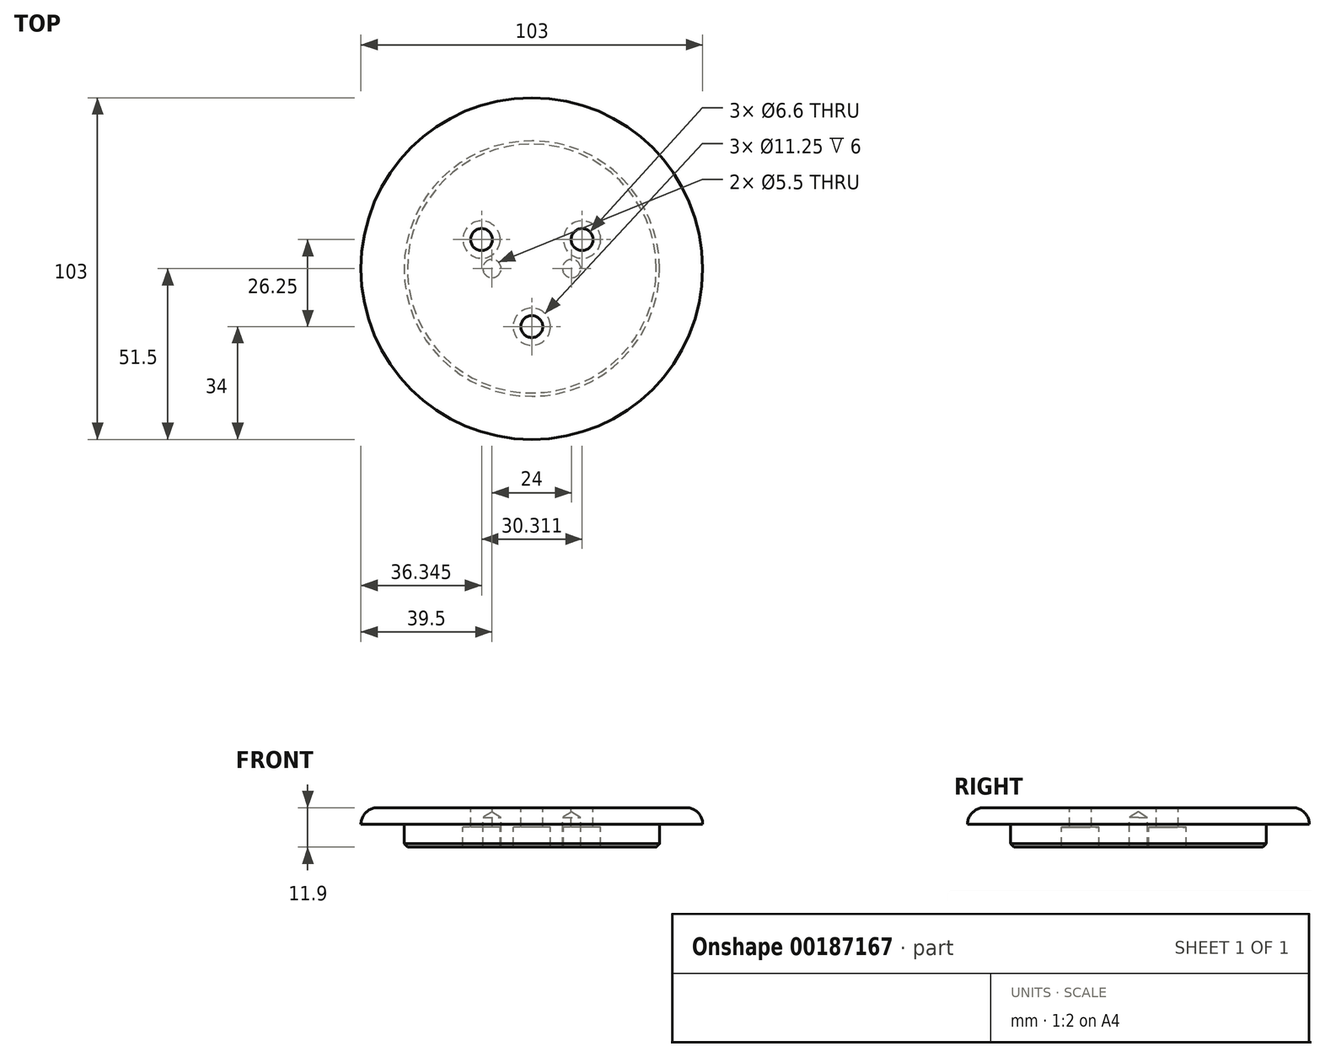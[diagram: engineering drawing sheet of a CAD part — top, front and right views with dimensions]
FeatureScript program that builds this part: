
annotation { "Feature Type Name" : "Feature", "Feature Type Description" : "" }
export const myFeature = defineFeature(function(context is Context, id is Id, definition is map)
    precondition{}
    {
        {
            var Q0;
            Q0=qCreatedBy(makeId("Top.planeOp"),FACE);
            var sketch = newSketch(context, id + "F0", { "sketchPlane" : qUnion([Q0])});
            skCircle(sketch, "E0", {"center": v(0, 0) * mm, "radius": 38.5 * mm});
            skCircle(sketch, "E1", {"center": v(0, 0) * mm, "radius": 51.5 * mm});
            skSolve(sketch);
        }
        {
            var Q0;
            Q0=makeQuery(id+"F0.imprint","IMPRINT",FACE,{"disambiguationData":[TD([[makeQuery(id+"F0.imprint","IMPRINT",EDGE,{"derivedFrom":sQuery(id+"F0.wireOp",EDGE,"E0")}),1.0]])]});
            extrude(context, id + "F1", {"entities" : qUnion([Q0]), "oppositeDirection" : true, "depth" : 6.9 * mm});
        }
        {
            var Q0;
            Q0=makeQuery(id+"F0.imprint","IMPRINT",FACE,{"disambiguationData":[TD([[makeQuery(id+"F0.imprint","IMPRINT",EDGE,{"derivedFrom":sQuery(id+"F0.wireOp",EDGE,"E0")}),-1.0]])]});
            var Q1;
            Q1=makeQuery(id+"F0.imprint","IMPRINT",FACE,{"disambiguationData":[TD([[makeQuery(id+"F0.imprint","IMPRINT",EDGE,{"derivedFrom":sQuery(id+"F0.wireOp",EDGE,"E0")}),1.0]])]});
            extrude(context, id + "F2", {"entities" : qUnion([Q0, Q1]), "operationType" : NewBodyOperationType.ADD, "depth" : 5 * mm});
        }
        {
            var Q0;
            Q0=makeQuery(id+"F1.opExtrude","CAP_FACE",FACE,{"disambiguationData":[OSD([sQuery(id+"F0.wireOp",EDGE,"E0")])],"isStart":false});
            var sketch = newSketch(context, id + "F3", { "sketchPlane" : qUnion([Q0])});
            skLineSegment(sketch, "E2", {"start": v(0, 0) * mm, "end": v(0, 17.5) * mm, "construction": true});
            skLineSegment(sketch, "E3.1.0", {"start": v(0, 0) * mm, "end": v(-15.16, -8.75) * mm, "construction": true});
            skLineSegment(sketch, "E3.2.0", {"start": v(0, 0) * mm, "end": v(15.16, -8.75) * mm, "construction": true});
            skPoint(sketch, "E3.center", {"position": v(0, 0) * mm});
            skSolve(sketch);
        }
        {
            var Q0;
            Q0=sQuery(id+"F3.wireOp",VERTEX,"E3.1.0.end");
            var Q1;
            Q1=sQuery(id+"F3.wireOp",VERTEX,"E2.end");
            var Q2;
            Q2=sQuery(id+"F3.wireOp",VERTEX,"E3.2.0.end");
            var Q3;
            Q3=makeQuery(id+"F1.opExtrude","SWEPT_BODY",BODY,{"disambiguationData":[OSD([sQuery(id+"F0.wireOp",EDGE,"E0")])]});
            hole(context, id + "F4", {"style" : HoleStyle.C_BORE, "holeDiameter" : 6.6 * mm, "cBoreDiameter" : 11.25 * mm, "cBoreDepth" : 6 * mm, "endStyle" : HoleEndStyle.THROUGH, "locations" : qUnion([Q0, Q1, Q2]), "scope" : qUnion([Q3]), "standardTappedOrClearance" : lookupTablePath({ "standard" : "ISO", "fit" : "Normal", "size" : "M6", "type" : "Clearance" }), "standardBlindInLast" : lookupTablePath({ "fit" : "Standard", "standard" : "ISO", "size" : "M6", "type" : "Clearance" }), "isTappedThrough" : true, "startStyle" : HoleStartStyle.PART});
        }
        {
            var Q0;
            Q0=makeQuery(id+"F1.opExtrude","CAP_FACE",FACE,{"disambiguationData":[OSD([sQuery(id+"F0.wireOp",EDGE,"E0")])],"isStart":false});
            var sketch = newSketch(context, id + "F5", { "sketchPlane" : qUnion([Q0])});
            skLineSegment(sketch, "E4", {"start": v(0, 0) * mm, "end": v(-12, 0) * mm, "construction": true});
            skLineSegment(sketch, "E5", {"start": v(0, 0) * mm, "end": v(0, -6.63) * mm, "construction": true});
            skLineSegment(sketch, "E6.MirrorCS", {"start": v(0, 0) * mm, "end": v(12, 0) * mm, "construction": true});
            skSolve(sketch);
        }
        {
            var Q0;
            Q0=sQuery(id+"F5.wireOp",VERTEX,"E4.end");
            var Q1;
            Q1=sQuery(id+"F5.wireOp",VERTEX,"E6.MirrorCS.end");
            var Q2;
            Q2=makeQuery(id+"F1.opExtrude","SWEPT_BODY",BODY,{"disambiguationData":[OSD([sQuery(id+"F0.wireOp",EDGE,"E0")])]});
            hole(context, id + "F6", {"style" : HoleStyle.SIMPLE, "holeDiameter" : 5.5 * mm, "endStyle" : HoleEndStyle.BLIND, "holeDepth" : 9 * mm, "locations" : qUnion([Q0, Q1]), "scope" : qUnion([Q2]), "startStyle" : HoleStartStyle.PART});
        }
        {
            var Q0;
            Q0=makeQuery(id+"F2.opExtrude","CAP_EDGE",EDGE,{"disambiguationData":[OSD([sQuery(id+"F0.wireOp",EDGE,"E1")])],"isStart":false});
            fillet(context, id + "F7", {"entities" : qUnion([Q0]), "radius" : 5 * mm, "tangentPropagation" : true, "allowEdgeOverflow" : false});
        }
        {
            var Q0;
            Q0=makeQuery(id+"F1.opExtrude","CAP_EDGE",EDGE,{"disambiguationData":[OSD([sQuery(id+"F0.wireOp",EDGE,"E0")])],"isStart":false});
            chamfer(context, id + "F8", {"entities" : qUnion([Q0]), "width" : 1 * mm, "tangentPropagation" : true});
        }
    });
